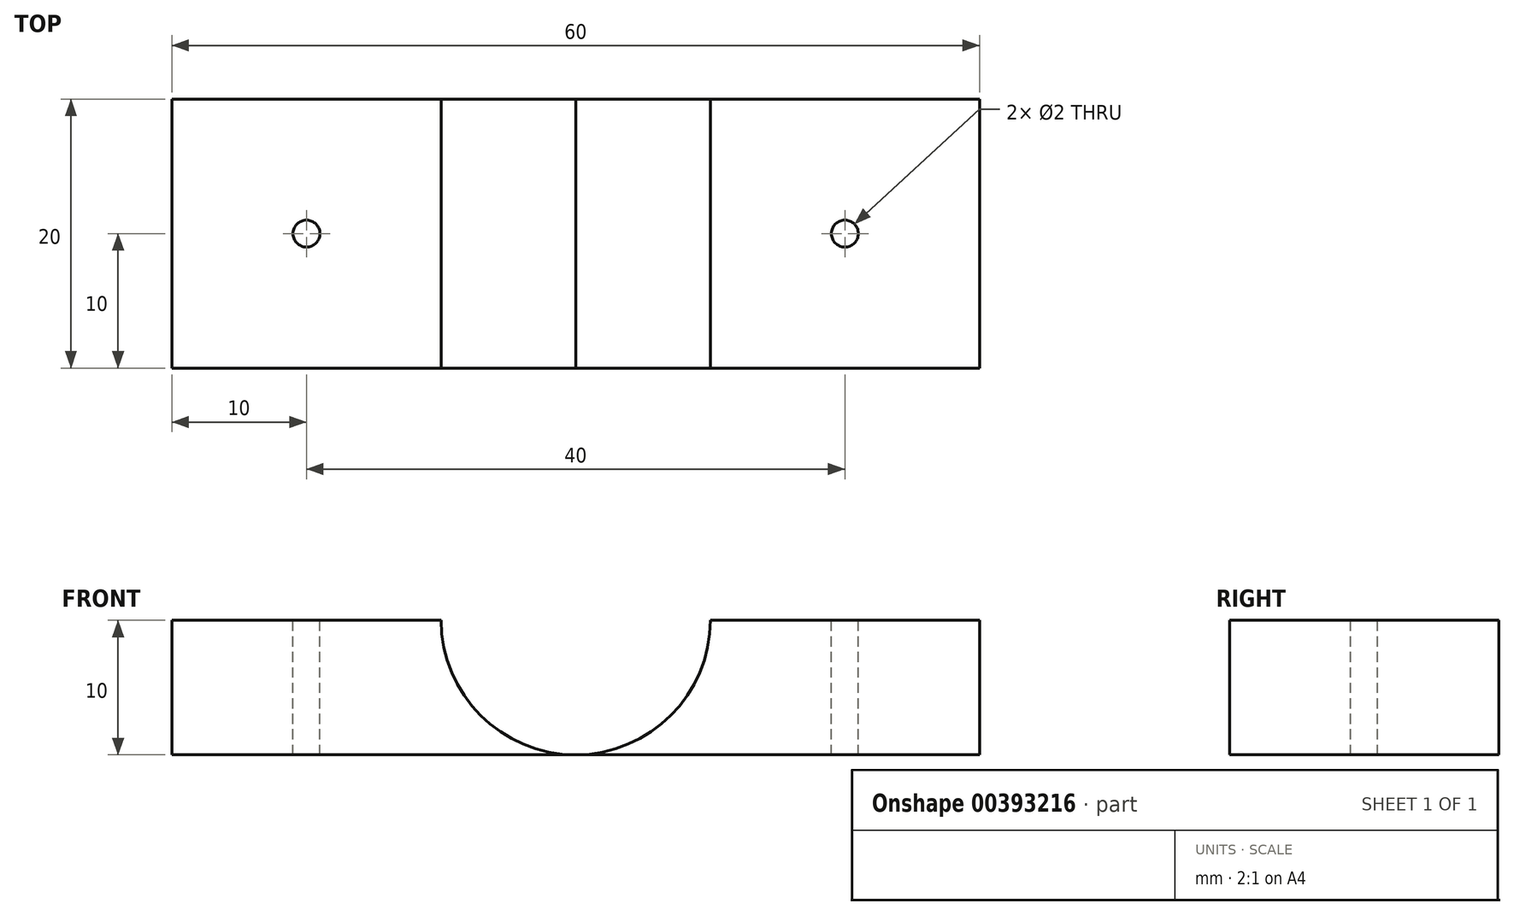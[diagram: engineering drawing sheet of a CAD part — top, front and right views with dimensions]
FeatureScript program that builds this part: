
annotation { "Feature Type Name" : "Feature", "Feature Type Description" : "" }
export const myFeature = defineFeature(function(context is Context, id is Id, definition is map)
    precondition{}
    {
        {
            var Q0;
            Q0=qCreatedBy(makeId("Front.planeOp"),FACE);
            var sketch = newSketch(context, id + "F0", { "sketchPlane" : qUnion([Q0])});
            skLineSegment(sketch, "E0.bottom", {"start": v(30, 5) * mm, "end": v(-30, 5) * mm});
            skLineSegment(sketch, "E0.top", {"start": v(30, -5) * mm, "end": v(-30, -5) * mm});
            skLineSegment(sketch, "E0.left", {"start": v(30, 5) * mm, "end": v(30, -5) * mm});
            skLineSegment(sketch, "E0.right", {"start": v(-30, 5) * mm, "end": v(-30, -5) * mm});
            skPoint(sketch, "E0.middle", {"position": v(0, 0) * mm});
            skCircle(sketch, "E1", {"center": v(0, 5) * mm, "radius": 5.07 * mm});
            skCircle(sketch, "E2", {"center": v(0, 5) * mm, "radius": 10 * mm});
            skSolve(sketch);
        }
        {
            var Q0;
            {var subQ0=sQuery(id+"F0.wireOp",EDGE,"E0.left");Q0=makeQuery(id+"F0.imprint","IMPRINT",FACE,{"disambiguationData":[TD([[makeQuery(id+"F0.imprint","IMPRINT",EDGE,{"derivedFrom":subQ0}),-1.0]])]});}
            var Q1;
            {var subQ0=sQuery(id+"F0.wireOp",EDGE,"E0.right");Q1=makeQuery(id+"F0.imprint","IMPRINT",FACE,{"disambiguationData":[TD([[makeQuery(id+"F0.imprint","IMPRINT",EDGE,{"derivedFrom":subQ0}),1.0]])]});}
            var Q2;
            {var subQ0=sQuery(id+"F0.wireOp",EDGE,"E2");var subQ1=sQuery(id+"F0.wireOp",EDGE,"E0.bottom");var subQ4=makeQuery(id+"F0.imprint","INTERSECT",VERTEX,{"disambiguationData":[OD(0.0)],"derivedFrom":[subQ1,subQ0]});Q2=makeQuery(id+"F0.imprint","IMPRINT",FACE,{"disambiguationData":[TD([[makeQuery(id+"F0.imprint","IMPRINT",EDGE,{"disambiguationData":[TD([[subQ4,-1.0]])],"derivedFrom":subQ1}),1.0]])]});}
            var Q3;
            {var subQ0=sQuery(id+"F0.wireOp",EDGE,"E2");var subQ1=sQuery(id+"F0.wireOp",EDGE,"E0.bottom");var subQ2=makeQuery(id+"F0.imprint","INTERSECT",VERTEX,{"disambiguationData":[OD(0.0)],"derivedFrom":[subQ1,subQ0]});Q3=makeQuery(id+"F0.imprint","IMPRINT",FACE,{"disambiguationData":[TD([[makeQuery(id+"F0.imprint","IMPRINT",EDGE,{"disambiguationData":[TD([[subQ2,-1.0]])],"derivedFrom":subQ1}),-1.0]])]});}
            extrude(context, id + "F1", {"entities" : qUnion([Q0, Q1, Q2, Q3]), "depth" : 20 * mm});
        }
        {
            var Q0;
            {var subQ0=sQuery(id+"F0.wireOp",EDGE,"E0.bottom");Q0=makeQuery(id+"F1.opExtrude","SWEPT_FACE",FACE,{"disambiguationData":[OSD([subQ0]),TDD([makeQuery(id+"F0.imprint","IMPRINT",EDGE,{"disambiguationData":[TD([[makeQuery(id+"F0.imprint","INTERSECT",VERTEX,{"derivedFrom":[subQ0,sQuery(id+"F0.wireOp",EDGE,"E0.right")]}),1.0]])],"derivedFrom":subQ0})])]});}
            var sketch = newSketch(context, id + "F2", { "sketchPlane" : qUnion([Q0])});
            skCircle(sketch, "E3", {"center": v(-20, -10) * mm, "radius": 1 * mm});
            skSolve(sketch);
        }
        {
            var Q0;
            Q0 = qSketchRegion(id + "F2", true);
            extrude(context, id + "F3", {"entities" : qUnion([Q0]), "operationType" : NewBodyOperationType.REMOVE, "oppositeDirection" : true, "depth" : 25 * mm});
        }
        {
            var Q0;
            {var subQ0=sQuery(id+"F0.wireOp",EDGE,"E0.bottom");Q0=makeQuery(id+"F1.opExtrude","SWEPT_FACE",FACE,{"disambiguationData":[OSD([subQ0]),TDD([makeQuery(id+"F0.imprint","IMPRINT",EDGE,{"disambiguationData":[TD([[makeQuery(id+"F0.imprint","INTERSECT",VERTEX,{"derivedFrom":[subQ0,sQuery(id+"F0.wireOp",EDGE,"E0.left")]}),-1.0]])],"derivedFrom":subQ0})])]});}
            var sketch = newSketch(context, id + "F4", { "sketchPlane" : qUnion([Q0])});
            skCircle(sketch, "E4", {"center": v(20, -10) * mm, "radius": 1 * mm});
            skSolve(sketch);
        }
        {
            var Q0;
            Q0=makeQuery(id+"F4.imprint","IMPRINT",FACE,{"disambiguationData":[TD([[makeQuery(id+"F4.imprint","IMPRINT",EDGE,{"derivedFrom":sQuery(id+"F4.wireOp",EDGE,"E4")}),1.0]])]});
            extrude(context, id + "F5", {"entities" : qUnion([Q0]), "operationType" : NewBodyOperationType.REMOVE, "oppositeDirection" : true, "depth" : 25 * mm});
        }
    });
